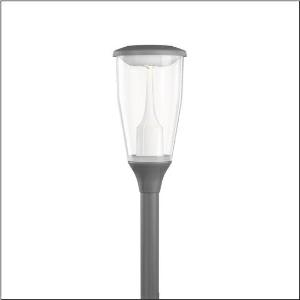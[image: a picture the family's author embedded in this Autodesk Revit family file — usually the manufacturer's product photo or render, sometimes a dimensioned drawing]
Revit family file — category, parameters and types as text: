
# Revit family: dl_11_iq___p1_0a_5xa5575nf14h000022_259a
name_source: partatom
category: Lighting Fixtures
units: mm (PartAtom-declared; Revit-internal decimal feet)

## family parameters
Cut with Voids When Loaded = No
Host = Face
Light Source = No
Part Type = Normal
Room Calculation Point = No
Round Connector Dimension = Use Diameter
Shared = No

## types (1)
- --- (1 x LED, 1530 lm, 11.8 W, 2700K)
    Apparent Load = 12 VA
    CIE Flux Codes = 34 63 91 95 100
    Color Rendering = 70
    Color Temperature = 2700K
    Default Elevation = 1800 mm
    Description = DL 11 iQ, mast luminaire, Module 540 iQ-SR, primary light control with 3 zone facetted reflector, of plastic, silver coated, highly specular, structured, primary optical cover: cover, of PMMA, transparent, light distribution: P1.0a, light emission: direct distribution, primary light characteristic: asymmetric, installation type: post-top, LED, High Power LED, rated luminous flux: 1.560lm, luminous efficacy: 149lm/W, light colour: 727, colour temperature: 2700K, control: Street-Remote, Auto-Match, Temp-Guard, Lumen-Switch, Night-Set, Smart-Wire, Light-Fading, Desk-Remote (wireless, voltage-free reading and setting of iQ features in the workshop via application-optimized NFC function/RFID function), optimised constant luminous flux control (CLO 2.0), mains connection: 220..240V, AC, 50/60Hz, connection cable pre-assembled, cable length: 5,5m, wiring characteristics: H07RN-F, 5-core, 1.5mm², start of lifetime: 12W, end of service life: 12W, reduction: 5W, luminaire housing, upper part, of diecast aluminium, coated, Siteco® metallic grey (DB 702S), spigot size: 76mm (post-top), post-top mast mounting element, of diecast aluminium, coated, Siteco® metallic grey (DB 702S), Module 540 iQ-SR, traffic white (RAL 9016), equipment: standard, protection rating (complete): IP66, insulation class (complete): insulation class II (safety insulation), certification: CE, ENEC, ENEC+, VDE, packaging unit: 1 piece

Light Distribution: P1.0a
    Height = 665 mm
    Lamp = 1 x LED
    Lamp Light Flux = 1530 lm
    Lamp Power = 11.8 W
    Lamp count = 1
    Length = 334 mm
    Luminous efficacy = 130 lm/W
    Manufacturer = Siteco
    ModVariant = No
    Model = 5XA5575NF14H000022
    Number of Poles = 1
    OnlyDefault = Yes
    Power Factor = 1
    Product Name = DL 11 iQ | P1.0a
    Product group = mast luminaire | pylon top
    ProductGroupID = 6100
    Protection Class = Protection class II
    Protection Degree = IP 66
    RLX_Detail_Level = 1
    RLX_Emergency_Light_Flux = 0 lm
    RLX_Emergency_Type = 0
    RLX_Emergency_Type_DB = No
    RlxData = <blob elided: 103557 chars, md5=09f86a92>
    Socket = socket
    Standby Power = 0 W
    System Light Flux = 1530 lm
    System Power = 12 W
    Type Comments = factory setting: luminous flux: 100 % | dim-lin: 254 | 472 mA
    Type Image = l_1258354.jpg
    URL = http://relux.com
    VarID = @adj_060471
    Voltage = 0 V
    Weight = 0.00 kg
    Width = 0 mm  [stored 0 ft]

note: [stored X ft] marks values corroborated as IEEE doubles in the binary element streams (Revit-internal decimal feet)

## geometry (parser evidence)
native form markers: Blend x4, Sweep x10
no freeform markers — native parametric forms only
